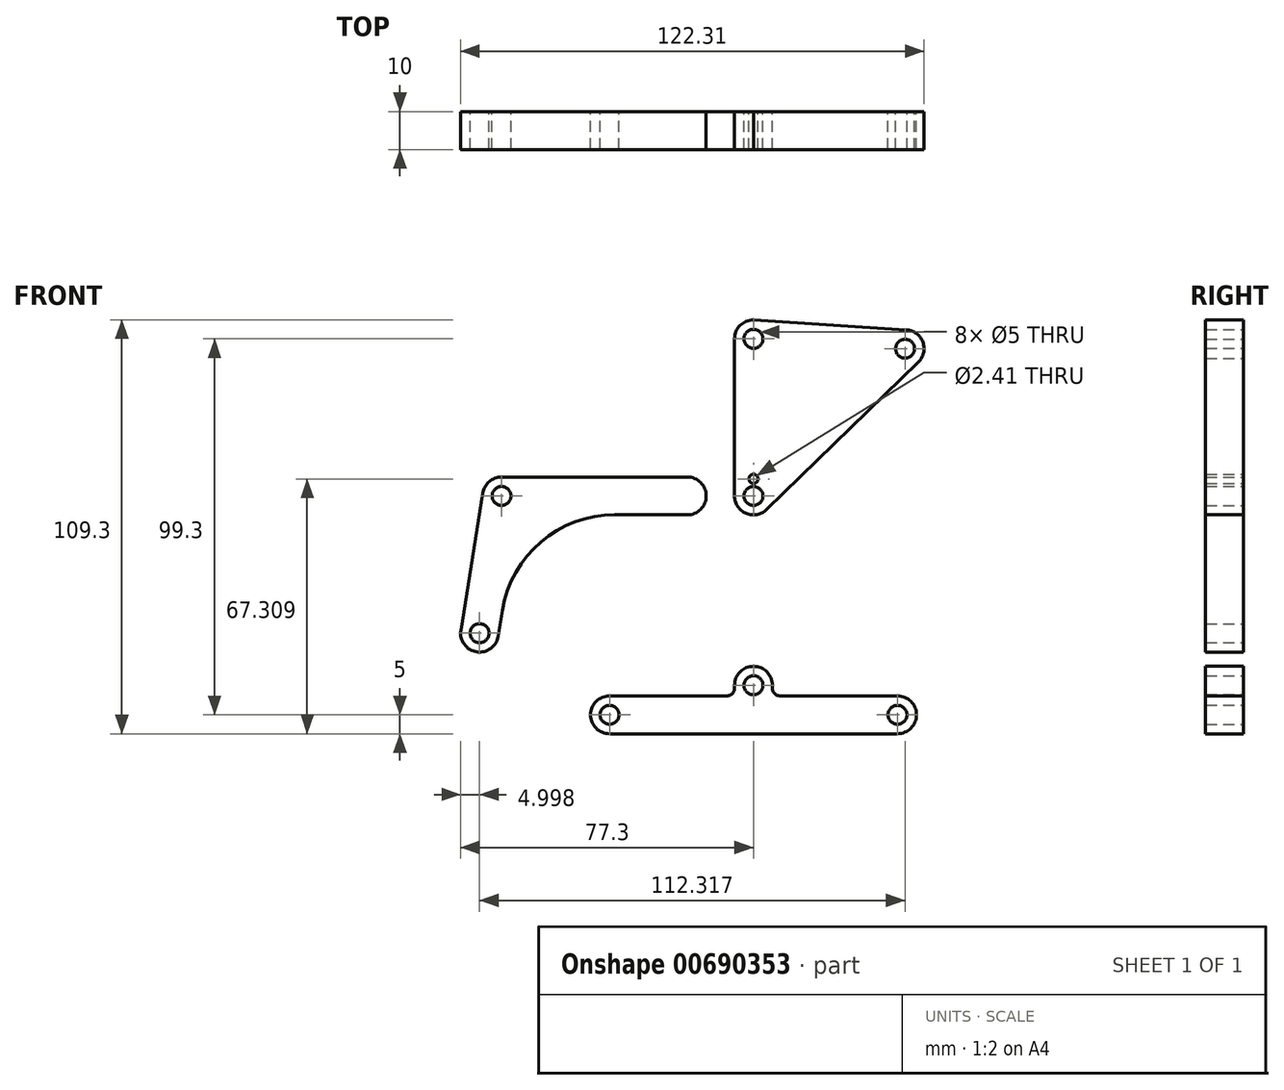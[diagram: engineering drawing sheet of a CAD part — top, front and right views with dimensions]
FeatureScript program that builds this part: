
annotation { "Feature Type Name" : "Feature", "Feature Type Description" : "" }
export const myFeature = defineFeature(function(context is Context, id is Id, definition is map)
    precondition{}
    {
        {
            var Q0;
            Q0=qCreatedBy(makeId("Front.planeOp"),FACE);
            var sketch = newSketch(context, id + "F0", { "sketchPlane" : qUnion([Q0])});
            skArc(sketch, "E0", {"start": v(0.65, 46.46) * mm, "mid": v(-3.3, 45.26) * mm, "end": v(-5, 41.5) * mm});
            skArc(sketch, "E1", {"start": v(-5, 0) * mm, "mid": v(-1.95, -4.6) * mm, "end": v(3.48, -3.59) * mm});
            skArc(sketch, "E2", {"start": v(43.5, 35.3) * mm, "mid": v(44.7, 40.62) * mm, "end": v(40.34, 43.88) * mm});
            skLineSegment(sketch, "E3", {"start": v(0, 46.5) * mm, "end": v(40.34, 43.88) * mm});
            skLineSegment(sketch, "E4", {"start": v(-5, 41.5) * mm, "end": v(-5, 0) * mm});
            skLineSegment(sketch, "E5", {"start": v(43.5, 35.3) * mm, "end": v(3.48, -3.59) * mm});
            skCircle(sketch, "E6", {"center": v(0, 41.5) * mm, "radius": 2.5 * mm});
            skCircle(sketch, "E7", {"center": v(0, 0) * mm, "radius": 2.5 * mm});
            skCircle(sketch, "E8", {"center": v(40.01, 38.9) * mm, "radius": 2.5 * mm});
            skCircle(sketch, "E9", {"center": v(0, 4.5) * mm, "radius": 1.2 * mm});
            skSolve(sketch);
        }
        {
            var Q0;
            Q0=makeQuery(id+"F0.imprint","IMPRINT",FACE,{"disambiguationData":[TD([[makeQuery(id+"F0.imprint","IMPRINT",EDGE,{"derivedFrom":sQuery(id+"F0.wireOp",EDGE,"E1")}),1.0]])]});
            extrude(context, id + "F1", {"entities" : qUnion([Q0]), "depth" : 10 * mm, "offsetDistance" : 25 * mm});
        }
        {
            var Q0;
            Q0=qCreatedBy(makeId("Front.planeOp"),FACE);
            var sketch = newSketch(context, id + "F2", { "sketchPlane" : qUnion([Q0])});
            skArc(sketch, "E10", {"start": v(-17.5, -5) * mm, "mid": v(-12.5, 0) * mm, "end": v(-17.5, 5) * mm});
            skArc(sketch, "E11", {"start": v(-77.24, -35.45) * mm, "mid": v(-73.1, -41.18) * mm, "end": v(-67.36, -37.03) * mm});
            skLineSegment(sketch, "E12", {"start": v(-77.24, -35.45) * mm, "end": v(-71.44, 0.8) * mm});
            skLineSegment(sketch, "E13", {"start": v(-66.5, 5) * mm, "end": v(-17.5, 5) * mm});
            skLineSegment(sketch, "E14", {"start": v(-67.36, -37.03) * mm, "end": v(-66.28, -30.26) * mm});
            skLineSegment(sketch, "E15", {"start": v(-17.5, -5) * mm, "end": v(-36.66, -5) * mm});
            skPoint(sketch, "E16.visualSharp", {"position": v(-62.24, -5) * mm});
            skArc(sketch, "E16.filletArc", {"start": v(-36.66, -5) * mm, "mid": v(-56.12, -12.17) * mm, "end": v(-66.28, -30.26) * mm});
            skCircle(sketch, "E17", {"center": v(-66.5, 0) * mm, "radius": 2.5 * mm});
            skCircle(sketch, "E18", {"center": v(-72.3, -36.24) * mm, "radius": 2.5 * mm});
            skArc(sketch, "E19", {"start": v(-66.5, 5) * mm, "mid": v(-69.74, 3.8) * mm, "end": v(-71.44, 0.8) * mm});
            skPoint(sketch, "E20.orphan", {"position": v(-71.56, 0) * mm});
            skSolve(sketch);
        }
        {
            var Q0;
            Q0=qCreatedBy(makeId("Front.planeOp"),FACE);
            var sketch = newSketch(context, id + "F3", { "sketchPlane" : qUnion([Q0])});
            skArc(sketch, "E21", {"start": v(-38, -52.8) * mm, "mid": v(-43, -57.8) * mm, "end": v(-38, -62.8) * mm});
            skArc(sketch, "E22", {"start": v(0, -45) * mm, "mid": v(-3.54, -46.46) * mm, "end": v(-5, -50) * mm});
            skLineSegment(sketch, "E23", {"start": v(-38, -52.8) * mm, "end": v(-7, -52.8) * mm});
            skLineSegment(sketch, "E24", {"start": v(-5, -50) * mm, "end": v(-5, -50.8) * mm});
            skPoint(sketch, "E25.visualSharp", {"position": v(-5, -52.8) * mm});
            skArc(sketch, "E25.filletArc", {"start": v(-7, -52.8) * mm, "mid": v(-5.59, -52.21) * mm, "end": v(-5, -50.8) * mm});
            skCircle(sketch, "E26", {"center": v(-38, -57.8) * mm, "radius": 2.5 * mm});
            skArc(sketch, "E27", {"start": v(0, -47.5) * mm, "mid": v(-2.5, -50) * mm, "end": v(0, -52.5) * mm});
            skLineSegment(sketch, "E28", {"start": v(-38, -62.8) * mm, "end": v(0, -62.8) * mm});
            skLineSegment(sketch, "E29.MirrorCS", {"start": v(5, -50) * mm, "end": v(5, -50.8) * mm});
            skArc(sketch, "E30.MirrorCS", {"start": v(7, -52.8) * mm, "mid": v(5.59, -52.21) * mm, "end": v(5, -50.8) * mm});
            skArc(sketch, "E31.MirrorCS", {"start": v(0, -45) * mm, "mid": v(3.54, -46.46) * mm, "end": v(5, -50) * mm});
            skLineSegment(sketch, "E32.MirrorCS", {"start": v(38, -52.8) * mm, "end": v(7, -52.8) * mm});
            skArc(sketch, "E33.MirrorCS", {"start": v(38, -52.8) * mm, "mid": v(43, -57.8) * mm, "end": v(38, -62.8) * mm});
            skPoint(sketch, "E34.MirrorP", {"position": v(5, -27.8) * mm});
            skCircle(sketch, "E35.MirrorC", {"center": v(38, -57.8) * mm, "radius": 2.5 * mm});
            skLineSegment(sketch, "E36.MirrorCS", {"start": v(38, -62.8) * mm, "end": v(0, -62.8) * mm});
            skArc(sketch, "E37.MirrorCS", {"start": v(0, -47.5) * mm, "mid": v(2.5, -50) * mm, "end": v(0, -52.5) * mm});
            skLineSegment(sketch, "E38", {"start": v(-38, -52.8) * mm, "end": v(-100, -52.8) * mm});
            skLineSegment(sketch, "E39", {"start": v(-100, -52.8) * mm, "end": v(-100, -62.8) * mm});
            skLineSegment(sketch, "E40", {"start": v(-100, -62.8) * mm, "end": v(-38, -62.8) * mm});
            skLineSegment(sketch, "E41.MirrorCS", {"start": v(38, -52.8) * mm, "end": v(100, -52.8) * mm});
            skLineSegment(sketch, "E42.MirrorCS", {"start": v(100, -52.8) * mm, "end": v(100, -62.8) * mm});
            skLineSegment(sketch, "E43.MirrorCS", {"start": v(100, -62.8) * mm, "end": v(38, -62.8) * mm});
            skSolve(sketch);
        }
        {
            var Q0;
            Q0=makeQuery(id+"F2.imprint","IMPRINT",FACE,{"disambiguationData":[TD([[makeQuery(id+"F2.imprint","IMPRINT",EDGE,{"derivedFrom":sQuery(id+"F2.wireOp",EDGE,"E10")}),1.0]])]});
            extrude(context, id + "F4", {"entities" : qUnion([Q0]), "depth" : 10 * mm, "offsetDistance" : 25 * mm});
        }
        {
            var Q0;
            Q0=makeQuery(id+"F3.imprint","IMPRINT",FACE,{"disambiguationData":[TD([[makeQuery(id+"F3.imprint","IMPRINT",EDGE,{"derivedFrom":sQuery(id+"F3.wireOp",EDGE,"E21")}),1.0]])]});
            extrude(context, id + "F5", {"entities" : qUnion([Q0]), "depth" : 10 * mm, "offsetDistance" : 25 * mm});
        }
    });
